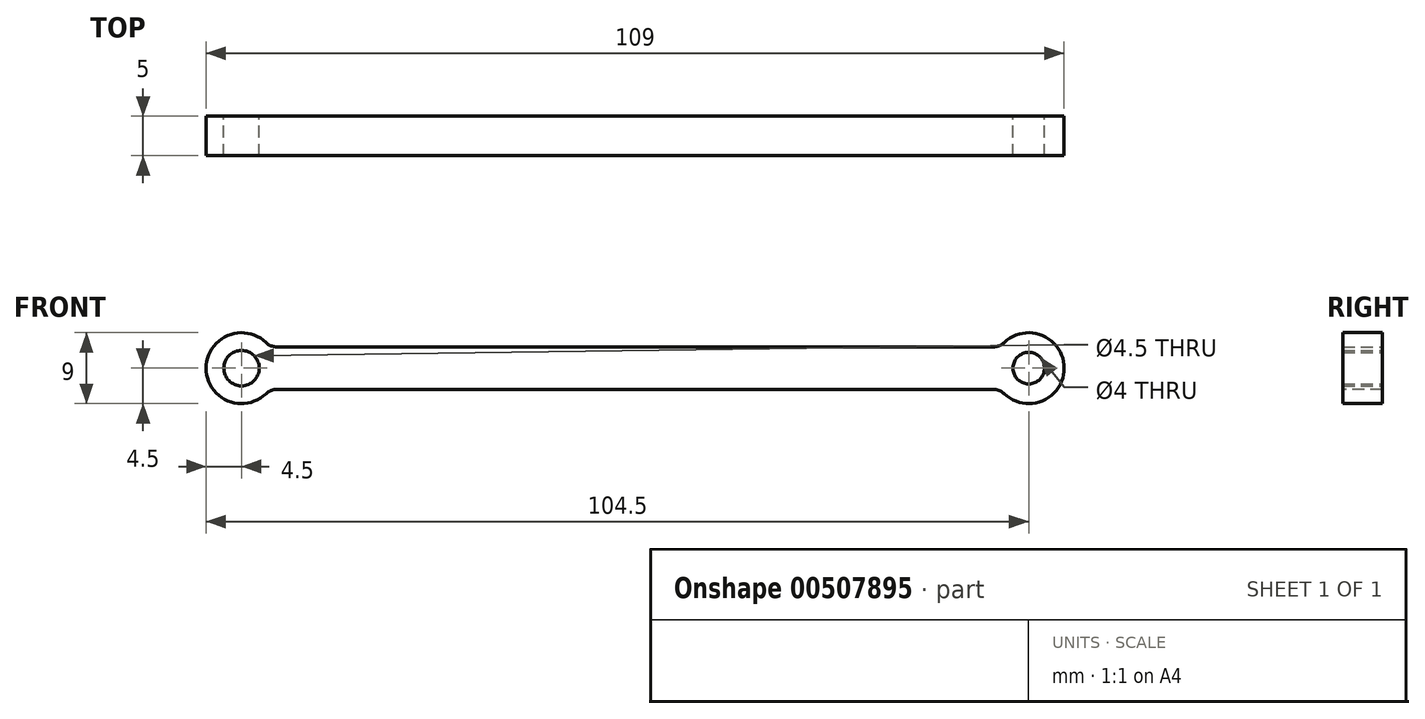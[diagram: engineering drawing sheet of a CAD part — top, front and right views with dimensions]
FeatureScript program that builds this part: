
annotation { "Feature Type Name" : "Feature", "Feature Type Description" : "" }
export const myFeature = defineFeature(function(context is Context, id is Id, definition is map)
    precondition{}
    {
        {
            var Q0;
            Q0=qCreatedBy(makeId("Front.planeOp"),FACE);
            var sketch = newSketch(context, id + "F0", { "sketchPlane" : qUnion([Q0])});
            skCircle(sketch, "E0", {"center": v(0, 0) * mm, "radius": 2.25 * mm});
            skCircle(sketch, "E1", {"center": v(0, 0) * mm, "radius": 4.5 * mm});
            skLineSegment(sketch, "E2", {"start": v(0, 0) * mm, "end": v(100, 0) * mm, "construction": true});
            skCircle(sketch, "E3", {"center": v(100, 0) * mm, "radius": 2 * mm});
            skCircle(sketch, "E4", {"center": v(100, 0) * mm, "radius": 4.5 * mm});
            skLineSegment(sketch, "E5", {"start": v(3.6, 2.7) * mm, "end": v(96.4, 2.7) * mm});
            skLineSegment(sketch, "E6.MirrorCS", {"start": v(3.6, -2.7) * mm, "end": v(96.4, -2.7) * mm});
            skSolve(sketch);
        }
        {
            var Q0;
            Q0=makeQuery(id+"F0.imprint","IMPRINT",FACE,{"disambiguationData":[TD([[makeQuery(id+"F0.imprint","IMPRINT",EDGE,{"derivedFrom":sQuery(id+"F0.wireOp",EDGE,"E0")}),-1.0]])]});
            var Q1;
            {var subQ0=sQuery(id+"F0.wireOp",EDGE,"E5");Q1=makeQuery(id+"F0.imprint","IMPRINT",FACE,{"disambiguationData":[TD([[makeQuery(id+"F0.imprint","IMPRINT",EDGE,{"derivedFrom":subQ0}),-1.0]])]});}
            var Q2;
            Q2=makeQuery(id+"F0.imprint","IMPRINT",FACE,{"disambiguationData":[TD([[makeQuery(id+"F0.imprint","IMPRINT",EDGE,{"derivedFrom":sQuery(id+"F0.wireOp",EDGE,"E3")}),-1.0]])]});
            extrude(context, id + "F1", {"entities" : qUnion([Q0, Q1, Q2]), "depth" : 5 * mm, "offsetDistance" : 25 * mm, "symmetric" : true});
        }
        {
            var Q0;
            Q0=makeQuery(id+"F1.opExtrude","SWEPT_EDGE",EDGE,{"disambiguationData":[OSD([sQuery(id+"F0.wireOp",EDGE,"E1"),sQuery(id+"F0.wireOp",EDGE,"E5")])]});
            var Q1;
            Q1=makeQuery(id+"F1.opExtrude","SWEPT_EDGE",EDGE,{"disambiguationData":[OSD([sQuery(id+"F0.wireOp",EDGE,"E4"),sQuery(id+"F0.wireOp",EDGE,"E5")])]});
            var Q2;
            Q2=makeQuery(id+"F1.opExtrude","SWEPT_EDGE",EDGE,{"disambiguationData":[OSD([sQuery(id+"F0.wireOp",EDGE,"E1"),sQuery(id+"F0.wireOp",EDGE,"E6.MirrorCS")])]});
            var Q3;
            Q3=makeQuery(id+"F1.opExtrude","SWEPT_EDGE",EDGE,{"disambiguationData":[OSD([sQuery(id+"F0.wireOp",EDGE,"E4"),sQuery(id+"F0.wireOp",EDGE,"E6.MirrorCS")])]});
            fillet(context, id + "F2", {"entities" : qUnion([Q0, Q1, Q2, Q3]), "radius" : 2 * mm, "tangentPropagation" : true, "allowEdgeOverflow" : false});
        }
    });
